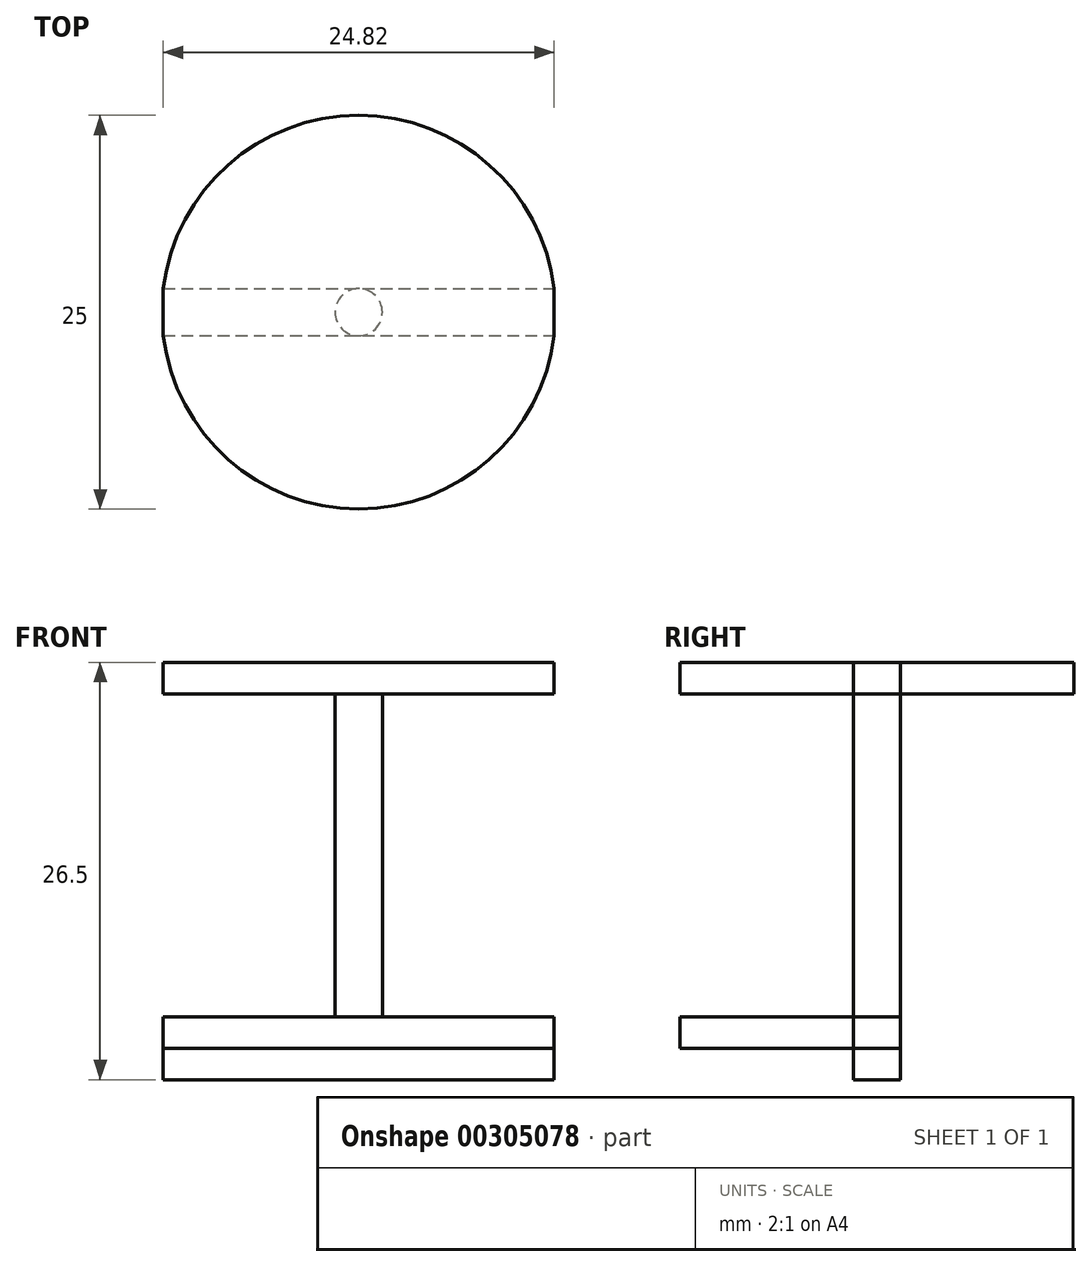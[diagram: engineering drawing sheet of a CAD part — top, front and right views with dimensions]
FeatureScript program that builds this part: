
annotation { "Feature Type Name" : "Feature", "Feature Type Description" : "" }
export const myFeature = defineFeature(function(context is Context, id is Id, definition is map)
    precondition{}
    {
        {
            var Q0;
            Q0=qCreatedBy(makeId("Top.planeOp"),FACE);
            var sketch = newSketch(context, id + "F0", { "sketchPlane" : qUnion([Q0])});
            skCircle(sketch, "E0", {"center": v(0, 0) * mm, "radius": 1.5 * mm});
            skCircle(sketch, "E1", {"center": v(0, 0) * mm, "radius": 12.5 * mm});
            skLineSegment(sketch, "E2", {"start": v(-13, 0) * mm, "end": v(14.82, 0) * mm});
            skLineSegment(sketch, "E3.bottom", {"start": v(-12.4, 1.5) * mm, "end": v(12.4, 1.5) * mm});
            skLineSegment(sketch, "E3.top", {"start": v(-12.4, -1.5) * mm, "end": v(12.4, -1.5) * mm});
            skLineSegment(sketch, "E3.left", {"start": v(-12.4, 1.5) * mm, "end": v(-12.4, -1.5) * mm});
            skLineSegment(sketch, "E3.right", {"start": v(12.4, 1.5) * mm, "end": v(12.4, -1.5) * mm});
            skSolve(sketch);
        }
        {
            var Q0;
            {var subQ0=sQuery(id+"F0.wireOp",EDGE,"E2");var subQ1=sQuery(id+"F0.wireOp",EDGE,"E0");var subQ2=makeQuery(id+"F0.imprint","INTERSECT",VERTEX,{"disambiguationData":[OD(0.0)],"derivedFrom":[subQ1,subQ0]});Q0=makeQuery(id+"F0.imprint","IMPRINT",FACE,{"disambiguationData":[TD([[makeQuery(id+"F0.imprint","IMPRINT",EDGE,{"disambiguationData":[TD([[subQ2,1.0]])],"derivedFrom":subQ1}),-1.0]])]});}
            var Q1;
            {var subQ0=sQuery(id+"F0.wireOp",EDGE,"E2");var subQ1=sQuery(id+"F0.wireOp",EDGE,"E0");var subQ2=makeQuery(id+"F0.imprint","INTERSECT",VERTEX,{"disambiguationData":[OD(0.0)],"derivedFrom":[subQ1,subQ0]});Q1=makeQuery(id+"F0.imprint","IMPRINT",FACE,{"disambiguationData":[TD([[makeQuery(id+"F0.imprint","IMPRINT",EDGE,{"disambiguationData":[TD([[subQ2,1.0]])],"derivedFrom":subQ1}),1.0]])]});}
            var Q2;
            {var subQ0=sQuery(id+"F0.wireOp",EDGE,"E2");var subQ1=sQuery(id+"F0.wireOp",EDGE,"E0");var subQ2=makeQuery(id+"F0.imprint","INTERSECT",VERTEX,{"disambiguationData":[OD(1.0)],"derivedFrom":[subQ1,subQ0]});Q2=makeQuery(id+"F0.imprint","IMPRINT",FACE,{"disambiguationData":[TD([[makeQuery(id+"F0.imprint","IMPRINT",EDGE,{"disambiguationData":[TD([[subQ2,-1.0]])],"derivedFrom":subQ1}),-1.0]])]});}
            var Q3;
            {var subQ0=sQuery(id+"F0.wireOp",EDGE,"E3.top");var subQ4=makeQuery(id+"F0.imprint","INTERSECT",VERTEX,{"derivedFrom":[sQuery(id+"F0.wireOp",EDGE,"E0"),subQ0]});Q3=makeQuery(id+"F0.imprint","IMPRINT",FACE,{"disambiguationData":[TD([[makeQuery(id+"F0.imprint","IMPRINT",EDGE,{"disambiguationData":[TD([[subQ4,1.0]])],"derivedFrom":subQ0}),-1.0]])]});}
            var Q4;
            {var subQ0=sQuery(id+"F0.wireOp",EDGE,"E3.bottom");var subQ1=sQuery(id+"F0.wireOp",EDGE,"E0");var subQ2=makeQuery(id+"F0.imprint","INTERSECT",VERTEX,{"derivedFrom":[subQ1,subQ0]});Q4=makeQuery(id+"F0.imprint","IMPRINT",FACE,{"disambiguationData":[TD([[makeQuery(id+"F0.imprint","IMPRINT",EDGE,{"disambiguationData":[TD([[subQ2,-1.0]])],"derivedFrom":subQ1}),-1.0]])]});}
            var Q5;
            {var subQ0=sQuery(id+"F0.wireOp",EDGE,"E3.bottom");var subQ1=sQuery(id+"F0.wireOp",EDGE,"E0");var subQ2=makeQuery(id+"F0.imprint","INTERSECT",VERTEX,{"derivedFrom":[subQ1,subQ0]});Q5=makeQuery(id+"F0.imprint","IMPRINT",FACE,{"disambiguationData":[TD([[makeQuery(id+"F0.imprint","IMPRINT",EDGE,{"disambiguationData":[TD([[subQ2,1.0]])],"derivedFrom":subQ1}),-1.0]])]});}
            var Q6;
            {var subQ0=sQuery(id+"F0.wireOp",EDGE,"E0");var subQ1=makeQuery(id+"F0.imprint","INTERSECT",VERTEX,{"derivedFrom":[subQ0,sQuery(id+"F0.wireOp",EDGE,"E3.bottom")]});Q6=makeQuery(id+"F0.imprint","IMPRINT",FACE,{"disambiguationData":[TD([[makeQuery(id+"F0.imprint","IMPRINT",EDGE,{"disambiguationData":[TD([[subQ1,1.0]])],"derivedFrom":subQ0}),1.0]])]});}
            extrude(context, id + "F1", {"entities" : qUnion([Q0, Q1, Q2, Q3, Q4, Q5, Q6]), "depth" : 2 * mm});
        }
        {
            var Q0;
            {var subQ0=sQuery(id+"F0.wireOp",EDGE,"E2");var subQ1=sQuery(id+"F0.wireOp",EDGE,"E0");var subQ2=makeQuery(id+"F0.imprint","INTERSECT",VERTEX,{"disambiguationData":[OD(0.0)],"derivedFrom":[subQ1,subQ0]});Q0=makeQuery(id+"F0.imprint","IMPRINT",FACE,{"disambiguationData":[TD([[makeQuery(id+"F0.imprint","IMPRINT",EDGE,{"disambiguationData":[TD([[subQ2,1.0]])],"derivedFrom":subQ1}),1.0]])]});}
            var Q1;
            {var subQ0=sQuery(id+"F0.wireOp",EDGE,"E2");var subQ1=sQuery(id+"F0.wireOp",EDGE,"E0");var subQ2=makeQuery(id+"F0.imprint","INTERSECT",VERTEX,{"disambiguationData":[OD(0.0)],"derivedFrom":[subQ1,subQ0]});Q1=makeQuery(id+"F0.imprint","IMPRINT",FACE,{"disambiguationData":[TD([[makeQuery(id+"F0.imprint","IMPRINT",EDGE,{"disambiguationData":[TD([[subQ2,-1.0]])],"derivedFrom":subQ1}),1.0]])]});}
            extrude(context, id + "F2", {"entities" : qUnion([Q0, Q1]), "depth" : 22.5 * mm, "hasSecondDirection" : true, "secondDirectionOppositeDirection" : false, "secondDirectionDepth" : 2 * mm});
        }
        {
            var Q0;
            {var subQ0=sQuery(id+"F0.wireOp",EDGE,"E2");var subQ1=sQuery(id+"F0.wireOp",EDGE,"E0");var subQ2=makeQuery(id+"F0.imprint","INTERSECT",VERTEX,{"disambiguationData":[OD(0.0)],"derivedFrom":[subQ1,subQ0]});Q0=makeQuery(id+"F0.imprint","IMPRINT",FACE,{"disambiguationData":[TD([[makeQuery(id+"F0.imprint","IMPRINT",EDGE,{"disambiguationData":[TD([[subQ2,-1.0]])],"derivedFrom":subQ1}),-1.0]])]});}
            var Q1;
            {var subQ0=sQuery(id+"F0.wireOp",EDGE,"E2");var subQ1=sQuery(id+"F0.wireOp",EDGE,"E0");var subQ2=makeQuery(id+"F0.imprint","INTERSECT",VERTEX,{"disambiguationData":[OD(0.0)],"derivedFrom":[subQ1,subQ0]});Q1=makeQuery(id+"F0.imprint","IMPRINT",FACE,{"disambiguationData":[TD([[makeQuery(id+"F0.imprint","IMPRINT",EDGE,{"disambiguationData":[TD([[subQ2,-1.0]])],"derivedFrom":subQ1}),1.0]])]});}
            var Q2;
            {var subQ0=sQuery(id+"F0.wireOp",EDGE,"E2");var subQ1=sQuery(id+"F0.wireOp",EDGE,"E0");var subQ2=makeQuery(id+"F0.imprint","INTERSECT",VERTEX,{"disambiguationData":[OD(0.0)],"derivedFrom":[subQ1,subQ0]});Q2=makeQuery(id+"F0.imprint","IMPRINT",FACE,{"disambiguationData":[TD([[makeQuery(id+"F0.imprint","IMPRINT",EDGE,{"disambiguationData":[TD([[subQ2,1.0]])],"derivedFrom":subQ1}),1.0]])]});}
            var Q3;
            {var subQ0=sQuery(id+"F0.wireOp",EDGE,"E2");var subQ1=sQuery(id+"F0.wireOp",EDGE,"E0");var subQ2=makeQuery(id+"F0.imprint","INTERSECT",VERTEX,{"disambiguationData":[OD(0.0)],"derivedFrom":[subQ1,subQ0]});Q3=makeQuery(id+"F0.imprint","IMPRINT",FACE,{"disambiguationData":[TD([[makeQuery(id+"F0.imprint","IMPRINT",EDGE,{"disambiguationData":[TD([[subQ2,1.0]])],"derivedFrom":subQ1}),-1.0]])]});}
            var Q4;
            {var subQ0=sQuery(id+"F0.wireOp",EDGE,"E2");var subQ1=sQuery(id+"F0.wireOp",EDGE,"E0");var subQ2=makeQuery(id+"F0.imprint","INTERSECT",VERTEX,{"disambiguationData":[OD(1.0)],"derivedFrom":[subQ1,subQ0]});Q4=makeQuery(id+"F0.imprint","IMPRINT",FACE,{"disambiguationData":[TD([[makeQuery(id+"F0.imprint","IMPRINT",EDGE,{"disambiguationData":[TD([[subQ2,-1.0]])],"derivedFrom":subQ1}),-1.0]])]});}
            var Q5;
            {var subQ0=sQuery(id+"F0.wireOp",EDGE,"E3.bottom");var subQ1=sQuery(id+"F0.wireOp",EDGE,"E0");var subQ2=makeQuery(id+"F0.imprint","INTERSECT",VERTEX,{"derivedFrom":[subQ1,subQ0]});Q5=makeQuery(id+"F0.imprint","IMPRINT",FACE,{"disambiguationData":[TD([[makeQuery(id+"F0.imprint","IMPRINT",EDGE,{"disambiguationData":[TD([[subQ2,-1.0]])],"derivedFrom":subQ1}),-1.0]])]});}
            var Q6;
            {var subQ0=sQuery(id+"F0.wireOp",EDGE,"E3.bottom");var subQ4=makeQuery(id+"F0.imprint","INTERSECT",VERTEX,{"derivedFrom":[sQuery(id+"F0.wireOp",EDGE,"E0"),subQ0]});Q6=makeQuery(id+"F0.imprint","IMPRINT",FACE,{"disambiguationData":[TD([[makeQuery(id+"F0.imprint","IMPRINT",EDGE,{"disambiguationData":[TD([[subQ4,1.0]])],"derivedFrom":subQ0}),1.0]])]});}
            var Q7;
            {var subQ0=sQuery(id+"F0.wireOp",EDGE,"E3.top");var subQ4=makeQuery(id+"F0.imprint","INTERSECT",VERTEX,{"derivedFrom":[sQuery(id+"F0.wireOp",EDGE,"E0"),subQ0]});Q7=makeQuery(id+"F0.imprint","IMPRINT",FACE,{"disambiguationData":[TD([[makeQuery(id+"F0.imprint","IMPRINT",EDGE,{"disambiguationData":[TD([[subQ4,1.0]])],"derivedFrom":subQ0}),-1.0]])]});}
            extrude(context, id + "F3", {"entities" : qUnion([Q0, Q1, Q2, Q3, Q4, Q5, Q6, Q7]), "depth" : 24.5 * mm, "hasSecondDirection" : true, "secondDirectionOppositeDirection" : false, "secondDirectionDepth" : 22.5 * mm});
        }
        {
            var Q0;
            {var subQ0=sQuery(id+"F0.wireOp",EDGE,"E3.bottom");var subQ1=sQuery(id+"F0.wireOp",EDGE,"E0");var subQ2=makeQuery(id+"F0.imprint","INTERSECT",VERTEX,{"derivedFrom":[subQ1,subQ0]});Q0=makeQuery(id+"F0.imprint","IMPRINT",FACE,{"disambiguationData":[TD([[makeQuery(id+"F0.imprint","IMPRINT",EDGE,{"disambiguationData":[TD([[subQ2,-1.0]])],"derivedFrom":subQ1}),-1.0]])]});}
            var Q1;
            {var subQ0=sQuery(id+"F0.wireOp",EDGE,"E3.bottom");var subQ1=sQuery(id+"F0.wireOp",EDGE,"E0");var subQ2=makeQuery(id+"F0.imprint","INTERSECT",VERTEX,{"derivedFrom":[subQ1,subQ0]});Q1=makeQuery(id+"F0.imprint","IMPRINT",FACE,{"disambiguationData":[TD([[makeQuery(id+"F0.imprint","IMPRINT",EDGE,{"disambiguationData":[TD([[subQ2,1.0]])],"derivedFrom":subQ1}),-1.0]])]});}
            var Q2;
            {var subQ0=sQuery(id+"F0.wireOp",EDGE,"E2");var subQ1=sQuery(id+"F0.wireOp",EDGE,"E0");var subQ2=makeQuery(id+"F0.imprint","INTERSECT",VERTEX,{"disambiguationData":[OD(0.0)],"derivedFrom":[subQ1,subQ0]});Q2=makeQuery(id+"F0.imprint","IMPRINT",FACE,{"disambiguationData":[TD([[makeQuery(id+"F0.imprint","IMPRINT",EDGE,{"disambiguationData":[TD([[subQ2,1.0]])],"derivedFrom":subQ1}),-1.0]])]});}
            var Q3;
            {var subQ0=sQuery(id+"F0.wireOp",EDGE,"E0");var subQ1=makeQuery(id+"F0.imprint","INTERSECT",VERTEX,{"derivedFrom":[subQ0,sQuery(id+"F0.wireOp",EDGE,"E3.bottom")]});Q3=makeQuery(id+"F0.imprint","IMPRINT",FACE,{"disambiguationData":[TD([[makeQuery(id+"F0.imprint","IMPRINT",EDGE,{"disambiguationData":[TD([[subQ1,1.0]])],"derivedFrom":subQ0}),1.0]])]});}
            var Q4;
            {var subQ0=sQuery(id+"F0.wireOp",EDGE,"E2");var subQ1=sQuery(id+"F0.wireOp",EDGE,"E0");var subQ2=makeQuery(id+"F0.imprint","INTERSECT",VERTEX,{"disambiguationData":[OD(1.0)],"derivedFrom":[subQ1,subQ0]});Q4=makeQuery(id+"F0.imprint","IMPRINT",FACE,{"disambiguationData":[TD([[makeQuery(id+"F0.imprint","IMPRINT",EDGE,{"disambiguationData":[TD([[subQ2,-1.0]])],"derivedFrom":subQ1}),1.0]])]});}
            var Q5;
            {var subQ0=sQuery(id+"F0.wireOp",EDGE,"E2");var subQ1=sQuery(id+"F0.wireOp",EDGE,"E0");var subQ2=makeQuery(id+"F0.imprint","INTERSECT",VERTEX,{"disambiguationData":[OD(1.0)],"derivedFrom":[subQ1,subQ0]});Q5=makeQuery(id+"F0.imprint","IMPRINT",FACE,{"disambiguationData":[TD([[makeQuery(id+"F0.imprint","IMPRINT",EDGE,{"disambiguationData":[TD([[subQ2,-1.0]])],"derivedFrom":subQ1}),-1.0]])]});}
            extrude(context, id + "F4", {"entities" : qUnion([Q0, Q1, Q2, Q3, Q4, Q5]), "oppositeDirection" : true, "depth" : 2 * mm});
        }
    });
